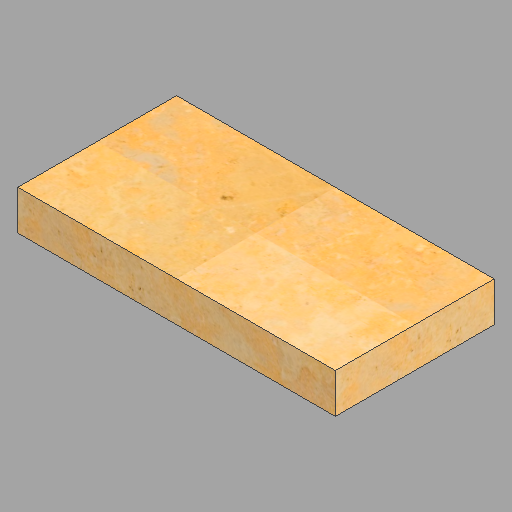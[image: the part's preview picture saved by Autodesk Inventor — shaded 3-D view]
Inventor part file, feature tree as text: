
AUTODESK INVENTOR PART (.ipt)
format: ipt  version: 2023 (Build 270158030, 158C)  size: 263,680 bytes
history: native  units: in
note: dims shown in document units (in); Inventor stores cm internally (conversion verified against a paired STEP export)
features: other x1, extrude x1, sketch x1
ambient origin geometry x8: Origin, YZ Plane, XZ Plane, XY Plane, X Axis, Y Axis, Z Axis, Center Point
bodies: Solid1 (feature_tree)
feature tree (3):
  other  "8X16X2 - 91"
  extrude  "Extrusion1"  Depth=8.0in
  sketch  "Sketch1"  dims[d0=16.0in d1=8.0in d2=2.0in d3=0.0in]
